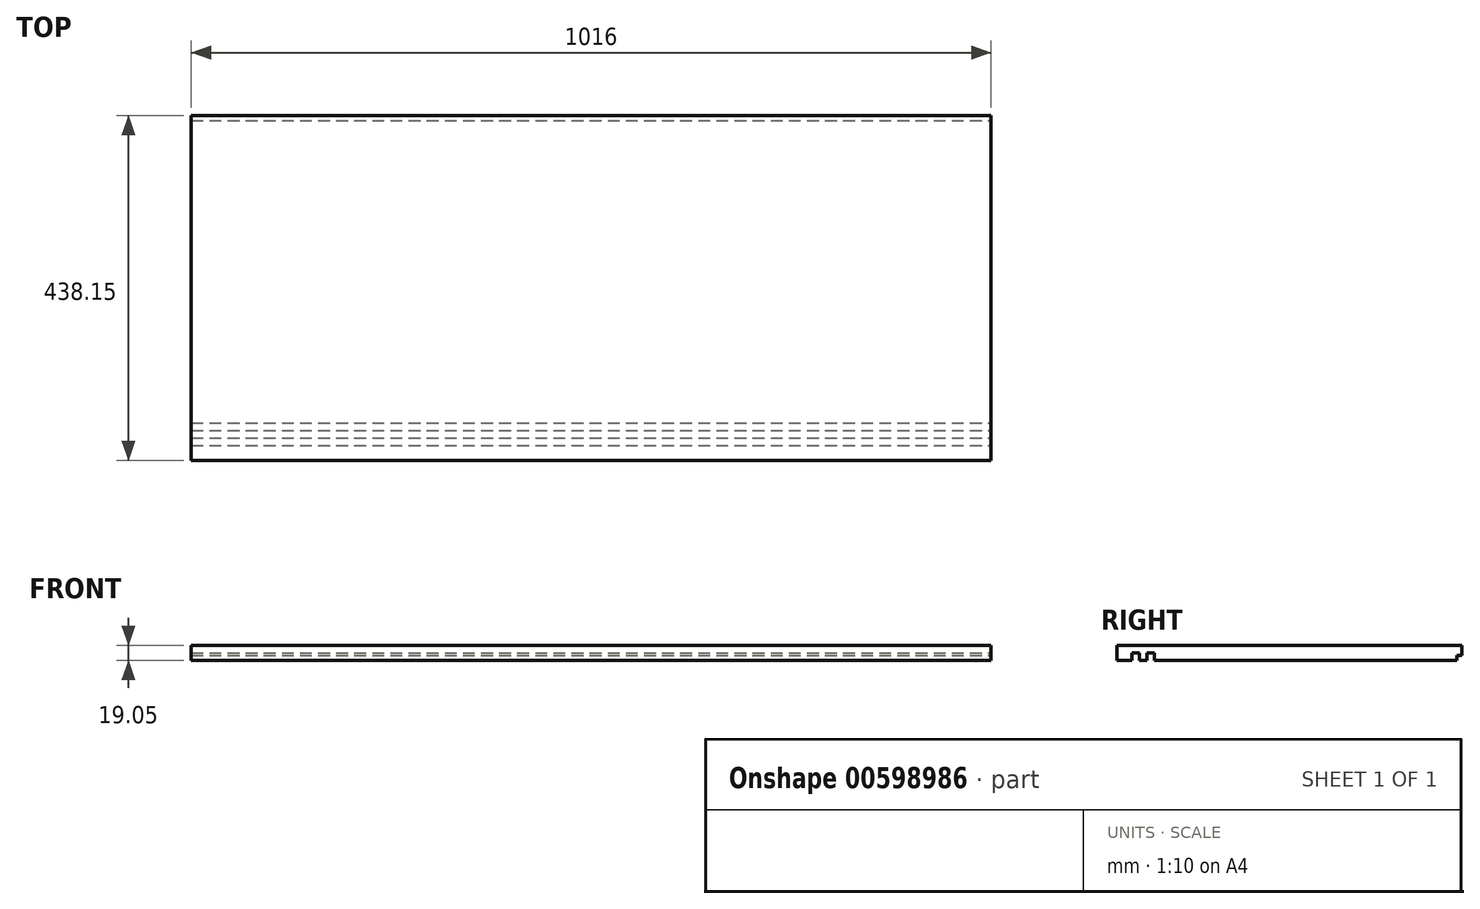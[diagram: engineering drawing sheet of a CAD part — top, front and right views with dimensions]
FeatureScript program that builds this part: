
annotation { "Feature Type Name" : "Feature", "Feature Type Description" : "" }
export const myFeature = defineFeature(function(context is Context, id is Id, definition is map)
    precondition{}
    {
        {
            var Q0;
            Q0=qCreatedBy(makeId("Top.planeOp"),FACE);
            var sketch = newSketch(context, id + "F0", { "sketchPlane" : qUnion([Q0])});
            skLineSegment(sketch, "E0.bottom", {"start": v(15.59, 14.12) * mm, "end": v(1031.59, 14.12) * mm});
            skLineSegment(sketch, "E0.top", {"start": v(15.59, 452.27) * mm, "end": v(1031.59, 452.27) * mm});
            skLineSegment(sketch, "E0.left", {"start": v(15.59, 14.12) * mm, "end": v(15.59, 452.27) * mm});
            skLineSegment(sketch, "E0.right", {"start": v(1031.59, 14.12) * mm, "end": v(1031.59, 452.27) * mm});
            skSolve(sketch);
        }
        {
            var Q0;
            Q0 = qSketchRegion(id + "F0", true);
            extrude(context, id + "F1", {"entities" : qUnion([Q0]), "depth" : 19.05 * mm, "offsetDistance" : 25.4 * mm});
        }
        {
            var Q0;
            Q0=makeQuery(id+"F1.opExtrude","CAP_FACE",FACE,{"disambiguationData":[OSD([sQuery(id+"F0.wireOp",EDGE,"E0.bottom"),sQuery(id+"F0.wireOp",EDGE,"E0.top"),sQuery(id+"F0.wireOp",EDGE,"E0.left"),sQuery(id+"F0.wireOp",EDGE,"E0.right")])],"isStart":true});
            var sketch = newSketch(context, id + "F2", { "sketchPlane" : qUnion([Q0])});
            skLineSegment(sketch, "E1.bottom", {"start": v(15.59, -42.7) * mm, "end": v(1031.59, -42.7) * mm});
            skLineSegment(sketch, "E1.top", {"start": v(15.59, -33.17) * mm, "end": v(1031.59, -33.17) * mm});
            skLineSegment(sketch, "E1.left", {"start": v(15.59, -42.7) * mm, "end": v(15.59, -33.17) * mm});
            skLineSegment(sketch, "E1.right", {"start": v(1031.59, -42.7) * mm, "end": v(1031.59, -33.17) * mm});
            skLineSegment(sketch, "E2.bottom", {"start": v(15.59, -52.22) * mm, "end": v(1031.59, -52.22) * mm});
            skLineSegment(sketch, "E2.top", {"start": v(15.59, -61.75) * mm, "end": v(1031.59, -61.75) * mm});
            skLineSegment(sketch, "E2.left", {"start": v(15.59, -52.22) * mm, "end": v(15.59, -61.75) * mm});
            skLineSegment(sketch, "E2.right", {"start": v(1031.59, -52.22) * mm, "end": v(1031.59, -61.75) * mm});
            skLineSegment(sketch, "E3", {"start": v(15.59, -42.7) * mm, "end": v(15.59, -52.22) * mm, "construction": true});
            skSolve(sketch);
        }
        {
            var Q0;
            Q0 = qSketchRegion(id + "F2", true);
            extrude(context, id + "F3", {"entities" : qUnion([Q0]), "operationType" : NewBodyOperationType.REMOVE, "oppositeDirection" : true, "depth" : 9.52 * mm, "offsetDistance" : 25.4 * mm});
        }
        {
            var Q0;
            {var subQ0=sQuery(id+"F0.wireOp",EDGE,"E0.top");var subQ1=sQuery(id+"F0.wireOp",EDGE,"E0.left");var subQ2=sQuery(id+"F0.wireOp",EDGE,"E0.right");Q0=makeQuery(id+"F3.boolean.opBoolean","SPLIT",FACE,{"disambiguationData":[TD([makeQuery(id+"F1.opExtrude","SWEPT_FACE",FACE,{"disambiguationData":[OSD([subQ0])]})])],"derivedFrom":makeQuery(id+"F1.opExtrude","CAP_FACE",FACE,{"disambiguationData":[OSD([sQuery(id+"F0.wireOp",EDGE,"E0.bottom"),subQ0,subQ1,subQ2])],"isStart":true})});}
            var sketch = newSketch(context, id + "F4", { "sketchPlane" : qUnion([Q0])});
            skLineSegment(sketch, "E4.bottom", {"start": v(15.59, -452.27) * mm, "end": v(1031.59, -452.27) * mm});
            skLineSegment(sketch, "E4.top", {"start": v(15.59, -445.92) * mm, "end": v(1031.59, -445.92) * mm});
            skLineSegment(sketch, "E4.left", {"start": v(15.59, -452.27) * mm, "end": v(15.59, -445.92) * mm});
            skLineSegment(sketch, "E4.right", {"start": v(1031.59, -452.27) * mm, "end": v(1031.59, -445.92) * mm});
            skSolve(sketch);
        }
        {
            var Q0;
            Q0 = qSketchRegion(id + "F4", true);
            extrude(context, id + "F5", {"entities" : qUnion([Q0]), "operationType" : NewBodyOperationType.REMOVE, "oppositeDirection" : true, "depth" : 6.35 * mm, "offsetDistance" : 25.4 * mm});
        }
    });
